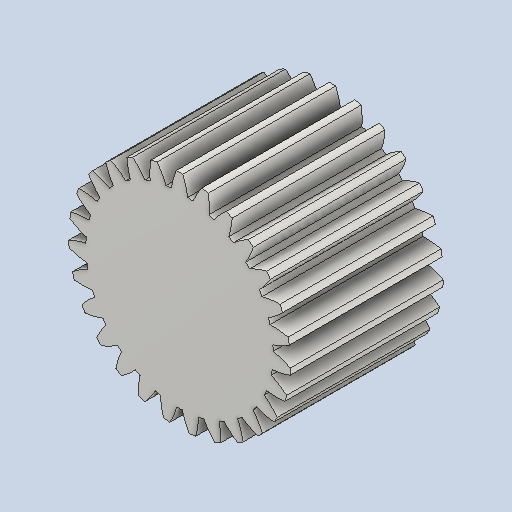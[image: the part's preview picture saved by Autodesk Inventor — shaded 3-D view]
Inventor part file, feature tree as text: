
AUTODESK INVENTOR PART (.ipt)
format: ipt  version: 2023 (Build 270158000, 158)  size: 285,696 bytes
history: native  units: mm (DEFAULTED — no unit token found)
features: plane x3, other x3, sketch x2, extrude x1
ambient origin geometry x8: Origin, YZ Plane, XZ Plane, XY Plane, X Axis, Y Axis, Z Axis, Center Point
bodies: Solid1 (feature_tree)
feature tree (9):
  extrude  "Extrusion1"  Depth=25.4mm TaperAngle=0.0deg
  plane  "Work Plane1"
  plane  "Work Plane2"
  plane  "Work Plane3"
  other  "Spur Gear"
  sketch  "Sketch1"  dims[d0=36.83mm d1=25.4mm d2=0.0mm]
  sketch  "Sketch2"  dims[d3=34.29mm d4=76.2mm d5=0.0mm d6=0.0mm d7=1.163553mm d9=0.0mm d14=0.0mm d15=27.305mm d16=0.0mm d17=0.0mm d18=0.0mm d19=27.305mm]
  other  "Srf1"
  other  "Pitch Diameter"
